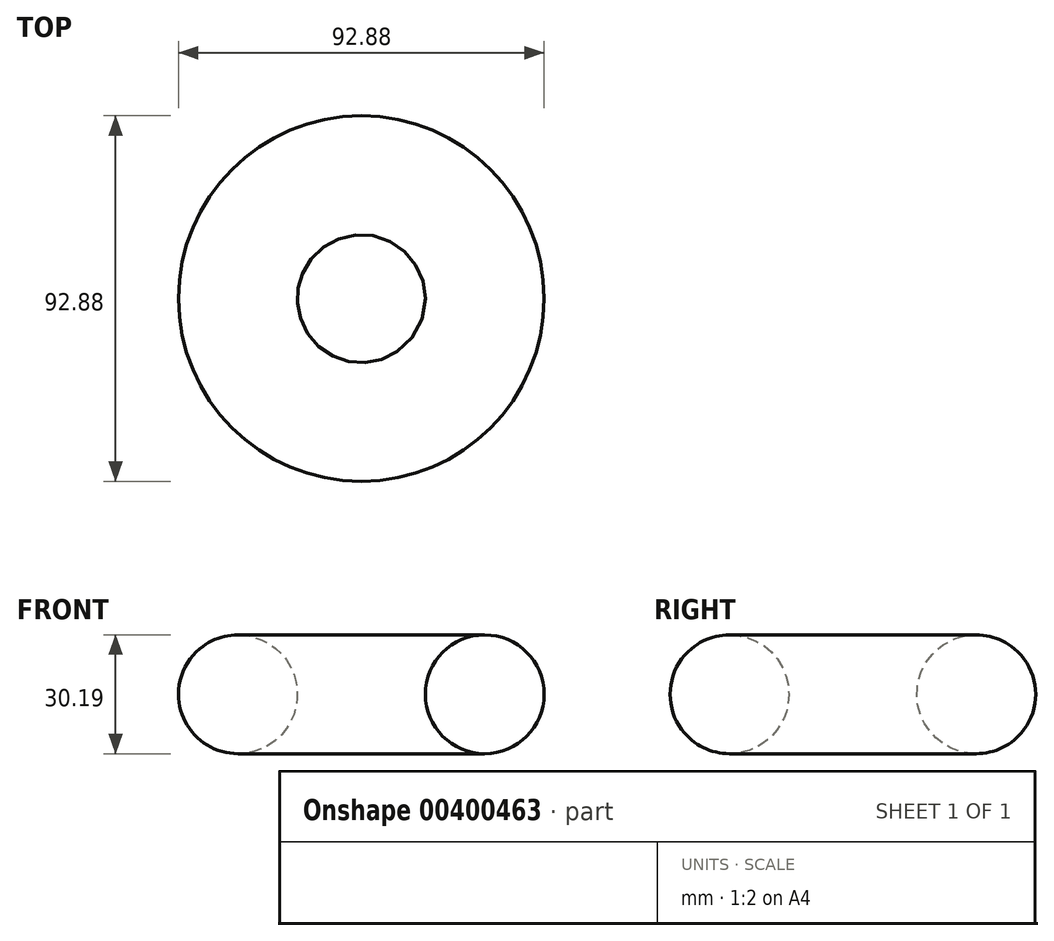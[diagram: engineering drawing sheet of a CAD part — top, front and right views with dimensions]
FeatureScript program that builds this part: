
annotation { "Feature Type Name" : "Feature", "Feature Type Description" : "" }
export const myFeature = defineFeature(function(context is Context, id is Id, definition is map)
    precondition{}
    {
        {
            var Q0;
            Q0=qCreatedBy(makeId("Front.planeOp"),FACE);
            var sketch = newSketch(context, id + "F0", { "sketchPlane" : qUnion([Q0])});
            skLineSegment(sketch, "E0", {"start": v(0, 76.5) * mm, "end": v(0, -76.69) * mm});
            skSolve(sketch);
        }
        {
            var Q0;
            Q0=qCreatedBy(makeId("Front.planeOp"),FACE);
            var sketch = newSketch(context, id + "F1", { "sketchPlane" : qUnion([Q0])});
            skCircle(sketch, "E1", {"center": v(31.35, 48.3) * mm, "radius": 15.1 * mm});
            skSolve(sketch);
        }
        {
            var Q0;
            Q0=makeQuery(id+"F1.imprint","IMPRINT",FACE,{"disambiguationData":[TD([[makeQuery(id+"F1.imprint","IMPRINT",EDGE,{"derivedFrom":sQuery(id+"F1.wireOp",EDGE,"E1")}),1.0]])]});
            var Q1;
            Q1=sQuery(id+"F0.wireOp",EDGE,"E0");
            revolve(context, id + "F2", {"entities" : qUnion([Q0]), "axis" : qUnion([Q1]), "revolveType" : RevolveType.FULL});
        }
    });
